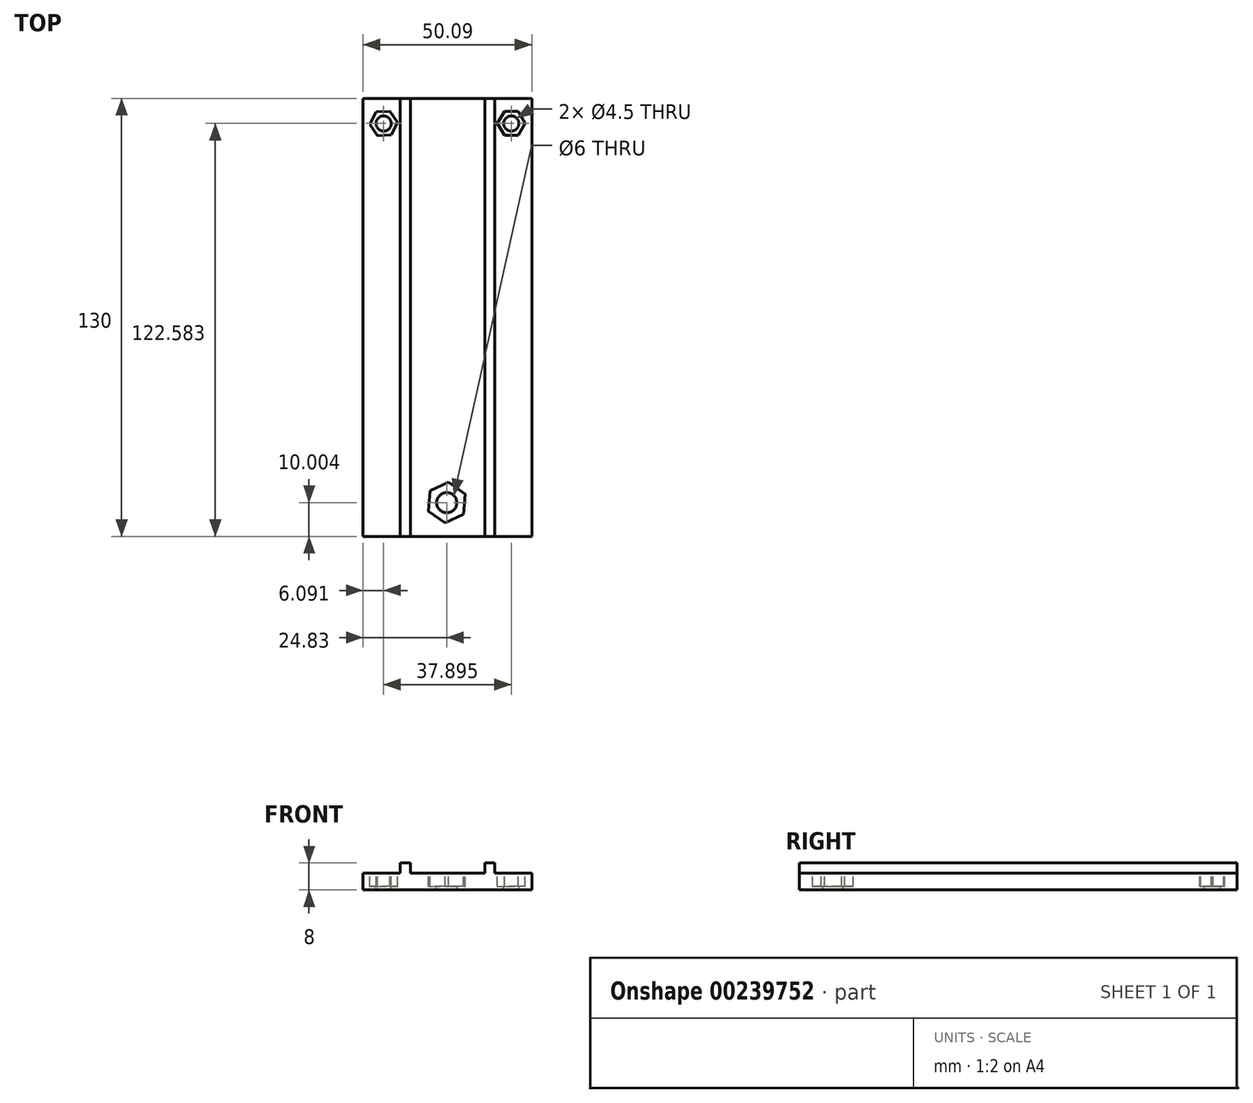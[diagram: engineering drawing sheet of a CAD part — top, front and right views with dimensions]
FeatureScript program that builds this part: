
annotation { "Feature Type Name" : "Feature", "Feature Type Description" : "" }
export const myFeature = defineFeature(function(context is Context, id is Id, definition is map)
    precondition{}
    {
        {
            var Q0;
            Q0=qCreatedBy(makeId("Top.planeOp"),FACE);
            var sketch = newSketch(context, id + "F0", { "sketchPlane" : qUnion([Q0])});
            skLineSegment(sketch, "E0.bottom", {"start": v(-35.81, 30.67) * mm, "end": v(14.28, 30.67) * mm});
            skLineSegment(sketch, "E0.top", {"start": v(-35.81, -99.33) * mm, "end": v(14.28, -99.33) * mm});
            skLineSegment(sketch, "E0.left", {"start": v(-35.81, 30.67) * mm, "end": v(-35.81, -99.33) * mm});
            skLineSegment(sketch, "E0.right", {"start": v(14.28, 30.67) * mm, "end": v(14.28, -99.33) * mm});
            skSolve(sketch);
        }
        {
            var Q0;
            Q0 = qSketchRegion(id + "F0", true);
            extrude(context, id + "F1", {"entities" : qUnion([Q0]), "depth" : 5 * mm});
        }
        {
            var Q0;
            Q0=makeQuery(id+"F1.opExtrude","CAP_FACE",FACE,{"disambiguationData":[OSD([sQuery(id+"F0.wireOp",EDGE,"E0.bottom"),sQuery(id+"F0.wireOp",EDGE,"E0.top"),sQuery(id+"F0.wireOp",EDGE,"E0.left"),sQuery(id+"F0.wireOp",EDGE,"E0.right")])],"isStart":false});
            var sketch = newSketch(context, id + "F2", { "sketchPlane" : qUnion([Q0])});
            skCircle(sketch, "E1.cCircle", {"center": v(8.18, 23.25) * mm, "radius": 3.55 * mm, "construction": true});
            skLineSegment(sketch, "E1.0", {"start": v(6.13, 26.8) * mm, "end": v(10.23, 26.8) * mm});
            skLineSegment(sketch, "E1.1", {"start": v(10.23, 26.8) * mm, "end": v(12.28, 23.25) * mm});
            skLineSegment(sketch, "E1.2", {"start": v(12.28, 23.25) * mm, "end": v(10.23, 19.7) * mm});
            skLineSegment(sketch, "E1.3", {"start": v(10.23, 19.7) * mm, "end": v(6.13, 19.7) * mm});
            skLineSegment(sketch, "E1.4", {"start": v(6.13, 19.7) * mm, "end": v(4.08, 23.25) * mm});
            skLineSegment(sketch, "E1.5", {"start": v(4.08, 23.25) * mm, "end": v(6.13, 26.8) * mm});
            skPoint(sketch, "E1.0.midPoint", {"position": v(8.18, 26.8) * mm});
            skCircle(sketch, "E2.cCircle", {"center": v(-29.72, 23.25) * mm, "radius": 3.55 * mm, "construction": true});
            skLineSegment(sketch, "E2.0", {"start": v(-33.81, 23) * mm, "end": v(-31.98, 26.67) * mm});
            skLineSegment(sketch, "E2.1", {"start": v(-31.98, 26.67) * mm, "end": v(-27.89, 26.92) * mm});
            skLineSegment(sketch, "E2.2", {"start": v(-27.89, 26.92) * mm, "end": v(-25.63, 23.5) * mm});
            skLineSegment(sketch, "E2.3", {"start": v(-25.63, 23.5) * mm, "end": v(-27.46, 19.83) * mm});
            skLineSegment(sketch, "E2.4", {"start": v(-27.46, 19.83) * mm, "end": v(-31.55, 19.59) * mm});
            skLineSegment(sketch, "E2.5", {"start": v(-31.55, 19.59) * mm, "end": v(-33.81, 23) * mm});
            skPoint(sketch, "E2.0.midPoint", {"position": v(-32.9, 24.84) * mm});
            skCircle(sketch, "E3", {"center": v(8.18, 23.25) * mm, "radius": 2.25 * mm});
            skCircle(sketch, "E4", {"center": v(-29.72, 23.25) * mm, "radius": 2.25 * mm});
            skLineSegment(sketch, "E5.bottom", {"start": v(-14.18, 30.67) * mm, "end": v(-7.78, 30.67) * mm});
            skLineSegment(sketch, "E5.top", {"start": v(-14.18, -99.33) * mm, "end": v(-7.78, -99.33) * mm});
            skCircle(sketch, "E6.cCircle", {"center": v(-10.98, -89.33) * mm, "radius": 5.25 * mm, "construction": true});
            skLineSegment(sketch, "E6.0", {"start": v(-15.93, -85.83) * mm, "end": v(-10.43, -83.29) * mm});
            skLineSegment(sketch, "E6.1", {"start": v(-10.43, -83.29) * mm, "end": v(-5.48, -86.79) * mm});
            skLineSegment(sketch, "E6.2", {"start": v(-5.48, -86.79) * mm, "end": v(-6.03, -92.82) * mm});
            skLineSegment(sketch, "E6.3", {"start": v(-6.03, -92.82) * mm, "end": v(-11.53, -95.36) * mm});
            skLineSegment(sketch, "E6.4", {"start": v(-11.53, -95.36) * mm, "end": v(-16.48, -91.87) * mm});
            skLineSegment(sketch, "E6.5", {"start": v(-16.48, -91.87) * mm, "end": v(-15.93, -85.83) * mm});
            skPoint(sketch, "E6.0.midPoint", {"position": v(-13.18, -84.56) * mm});
            skCircle(sketch, "E7", {"center": v(-10.98, -89.33) * mm, "radius": 3 * mm});
            skSolve(sketch);
        }
        {
            var Q0;
            Q0=makeQuery(id+"F2.imprint","IMPRINT",FACE,{"disambiguationData":[TD([[makeQuery(id+"F2.imprint","IMPRINT",EDGE,{"derivedFrom":sQuery(id+"F2.wireOp",EDGE,"E7")}),1.0]])]});
            var Q1;
            Q1=makeQuery(id+"F2.imprint","IMPRINT",FACE,{"disambiguationData":[TD([[makeQuery(id+"F2.imprint","IMPRINT",EDGE,{"derivedFrom":sQuery(id+"F2.wireOp",EDGE,"E3")}),1.0]])]});
            var Q2;
            Q2=makeQuery(id+"F2.imprint","IMPRINT",FACE,{"disambiguationData":[TD([[makeQuery(id+"F2.imprint","IMPRINT",EDGE,{"derivedFrom":sQuery(id+"F2.wireOp",EDGE,"E4")}),1.0]])]});
            extrude(context, id + "F3", {"entities" : qUnion([Q0, Q1, Q2]), "operationType" : NewBodyOperationType.REMOVE, "oppositeDirection" : true, "depth" : 25 * mm});
        }
        {
            var Q0;
            Q0 = qSketchRegion(id + "F2", true);
            extrude(context, id + "F4", {"entities" : qUnion([Q0]), "operationType" : NewBodyOperationType.REMOVE, "oppositeDirection" : true, "depth" : 4 * mm});
        }
        {
            var Q0;
            Q0=makeQuery(id+"F1.opExtrude","CAP_FACE",FACE,{"disambiguationData":[OSD([sQuery(id+"F0.wireOp",EDGE,"E0.bottom"),sQuery(id+"F0.wireOp",EDGE,"E0.top"),sQuery(id+"F0.wireOp",EDGE,"E0.left"),sQuery(id+"F0.wireOp",EDGE,"E0.right")])],"isStart":false});
            var sketch = newSketch(context, id + "F5", { "sketchPlane" : qUnion([Q0])});
            skLineSegment(sketch, "E8.bottom", {"start": v(3.28, 30.67) * mm, "end": v(0.28, 30.67) * mm});
            skLineSegment(sketch, "E8.top", {"start": v(3.28, -99.33) * mm, "end": v(0.28, -99.33) * mm});
            skLineSegment(sketch, "E8.left", {"start": v(3.28, 30.67) * mm, "end": v(3.28, -99.33) * mm});
            skLineSegment(sketch, "E8.right", {"start": v(0.28, 30.67) * mm, "end": v(0.28, -99.33) * mm});
            skLineSegment(sketch, "E9.bottom", {"start": v(-21.81, 30.67) * mm, "end": v(-24.81, 30.67) * mm});
            skLineSegment(sketch, "E9.top", {"start": v(-21.81, -99.33) * mm, "end": v(-24.81, -99.33) * mm});
            skLineSegment(sketch, "E9.left", {"start": v(-21.81, 30.67) * mm, "end": v(-21.81, -99.33) * mm});
            skLineSegment(sketch, "E9.right", {"start": v(-24.81, 30.67) * mm, "end": v(-24.81, -99.33) * mm});
            skSolve(sketch);
        }
        {
            var Q0;
            Q0 = qSketchRegion(id + "F5", true);
            extrude(context, id + "F6", {"entities" : qUnion([Q0]), "operationType" : NewBodyOperationType.ADD, "depth" : 3 * mm});
        }
    });
